# Revit family: HVAC_Mechanical-Ventilation_Envira-North_Altra-Air-Sailfin_Ceiling-Fan2
name_source: partatom
category: Electrical Fixtures
units: mm (PartAtom-declared; Revit-internal decimal feet)

## family parameters
Always vertical = No
Cut with Voids When Loaded = No
Maintain Annotation Orientation = No
OmniClass Number = 23.75.35.17.17.11
OmniClass Title = Ceiling Fans
Part Type = Normal
Room Calculation Point = No
Round Connector Dimension = Use Diameter
Shared = No
Work Plane-Based = Yes

## types (5) — shared parameters
Alternate Voltage = 460 V
CFEI 40% Speed = 1 ft³·h/(min·Btu)
Date Updated = 17/12/2024
Default Elevation = 0.00"
Description = Altra-Air Sailfin Fan
Manufacturer = Envira-North Systems
Number of Poles = 3
Power Factor = 1
Product Material = Envira North Systems - Metal
Product Page URL = https://www.enviranorth.com
Sound Rating = 62.5
URL = https://www.enviranorth.com
Version = 1
Voltage = 230 V
Wattage = 782 W
z_Clearence Blades = 30.00"
z_Clearence to Floor = 144.00"
z_Extension Mount 2FT = Extension Mount : 2FT
z_Extension Mount 4FT = Extension Mount : 4FT
z_Standard Mount 1FT = Mount Length : 1FT
z_Standard Mount 2FT = Mount Length : 2FT
z_Standard Mount 4FT = Mount Length : 4FT

## per-type parameters (varying)
| type | CFEI High Speed | Design Ventilation Air Flow | Diameter | Maximum Effective Diameter | Maximum Velocity | Model | Weight | z_Blades Length | z_Clearence Blades Diameter | z_Radius |
| EN675X5002 - 8FT | 1 ft³·h/(min·Btu) | 59494 CFM | 96.00" | 720.00" | 433 FPM | EN675X5002 | 220.00 lbf | Blade : 08FT | 132.00" | 48.00" |
| EN675X5006 - 12FT | 0 ft³·h/(min·Btu) | 70424 CFM | 144.00" | 960.00" | 512 FPM | EN675X5006 | 245.00 lbf | Blade : 12FT | 180.00" | 72.00" |
| EN675X5010 - 16FT | 1 ft³·h/(min·Btu) | 127033 CFM | 192.00" | 1680.00" | 422 FPM | EN675X5010 | 275.00 lbf | Blade : 16FT | 228.00" | 96.00" |
| EN675X5014 - 20FT | 1 ft³·h/(min·Btu) | 176200 CFM | 240.00" | 2400.00" | 439 FPM | EN675X5014 | 320.00 lbf | Blade : 20FT | 276.00" | 120.00" |
| EN675X5016 - 24FT | 1 ft³·h/(min·Btu) | 315026 CFM | 288.00" | 2760.00" | 497 FPM | EN675X5016 | 347.00 lbf | Blade : 24FT | 324.00" | 144.00" |

## geometry (parser evidence)
native form markers: Sweep x13
no freeform markers — native parametric forms only
